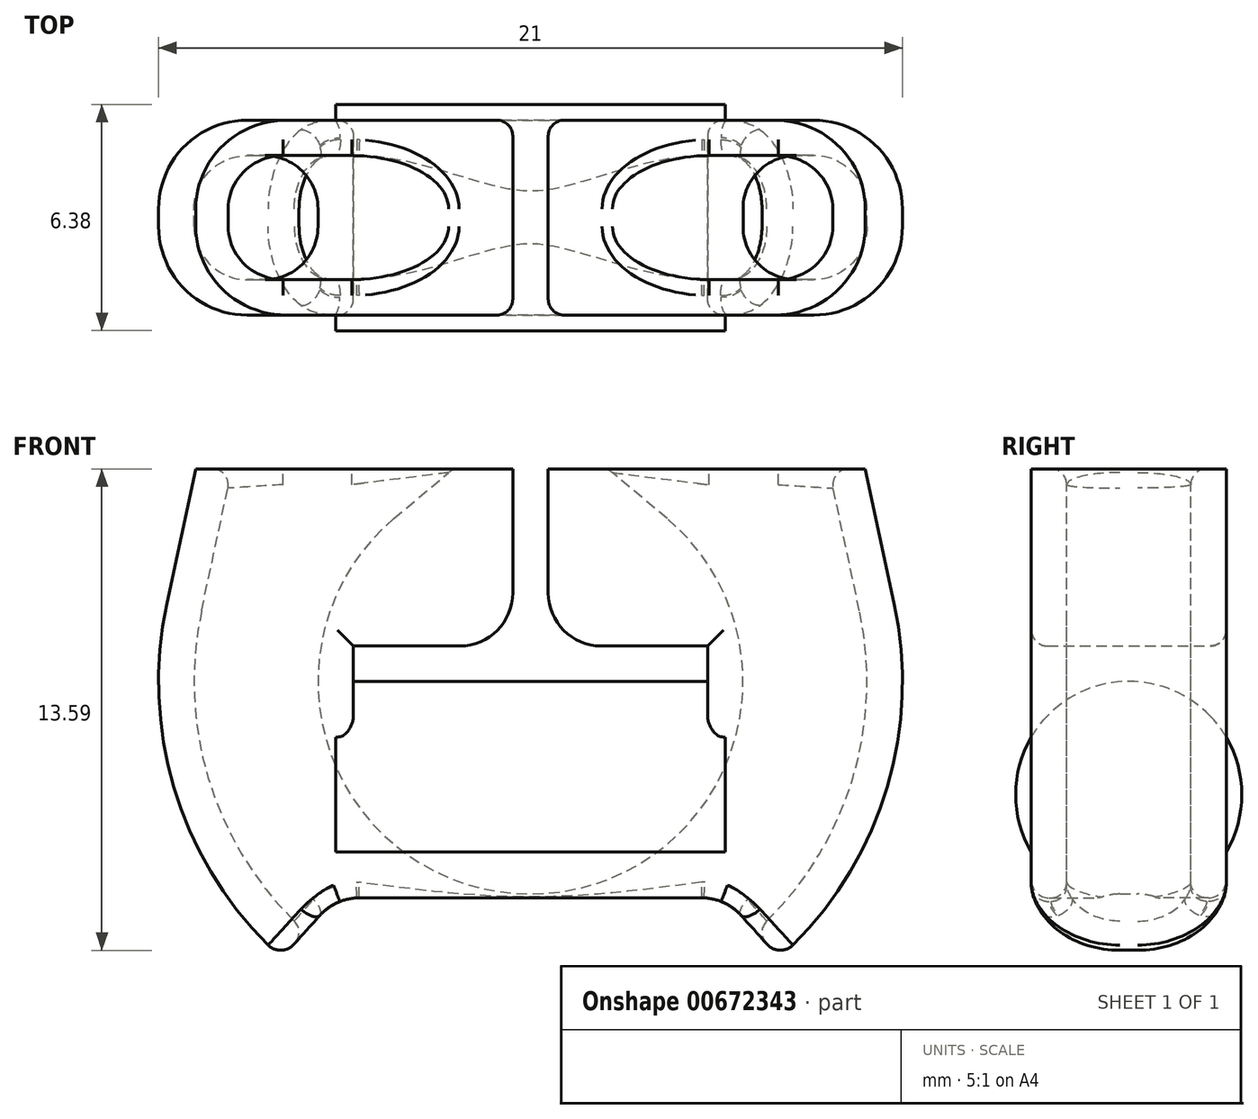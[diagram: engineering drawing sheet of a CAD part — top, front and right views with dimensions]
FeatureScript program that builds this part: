
annotation { "Feature Type Name" : "Feature", "Feature Type Description" : "" }
export const myFeature = defineFeature(function(context is Context, id is Id, definition is map)
    precondition{}
    {
        {
            var Q0;
            Q0=qCreatedBy(makeId("Front.planeOp"),FACE);
            var sketch = newSketch(context, id + "F0", { "sketchPlane" : qUnion([Q0])});
            skLineSegment(sketch, "E0.bottom", {"start": v(0, 0) * mm, "end": v(5, 0) * mm});
            skLineSegment(sketch, "E0.top", {"start": v(0, 1) * mm, "end": v(5, 1) * mm});
            skLineSegment(sketch, "E0.left", {"start": v(0, 0) * mm, "end": v(0, 1) * mm});
            skLineSegment(sketch, "E0.right", {"start": v(5, 0) * mm, "end": v(5, 1) * mm});
            skSolve(sketch);
        }
        {
            var Q0;
            Q0=qCreatedBy(makeId("Front.planeOp"),FACE);
            var sketch = newSketch(context, id + "F1", { "sketchPlane" : qUnion([Q0])});
            skArc(sketch, "E1", {"start": v(0, -10.5) * mm, "mid": v(8.17, -6.6) * mm, "end": v(10.27, 2.2) * mm});
            skLineSegment(sketch, "E2", {"start": v(10.27, 2.2) * mm, "end": v(9.45, 6) * mm});
            skLineSegment(sketch, "E3", {"start": v(9.45, 6) * mm, "end": v(0, 6) * mm});
            skLineSegment(sketch, "E4", {"start": v(0, 6) * mm, "end": v(0, -10.5) * mm});
            skPoint(sketch, "E5", {"position": v(10.5, 0) * mm});
            skPoint(sketch, "E6", {"position": v(0, 50) * mm});
            skSolve(sketch);
        }
        {
            var Q0;
            Q0=qSketchRegion(id+"F1",true);
            extrude(context, id + "F2", {"entities" : qUnion([Q0]), "depth" : 2.75 * mm, "offsetDistance" : 25 * mm});
        }
        {
            var Q0;
            Q0=qCreatedBy(makeId("Front.planeOp"),FACE);
            var sketch = newSketch(context, id + "F3", { "sketchPlane" : qUnion([Q0])});
            skArc(sketch, "E7", {"start": v(0, -6) * mm, "mid": v(5.64, -2.05) * mm, "end": v(3.86, 4.6) * mm});
            skArc(sketch, "E8.1", {"start": v(0, -9.5) * mm, "mid": v(7.39, -5.97) * mm, "end": v(9.29, 2) * mm});
            skLineSegment(sketch, "E9", {"start": v(9.29, 2) * mm, "end": v(8.43, 6) * mm});
            skLineSegment(sketch, "E10", {"start": v(3.86, 4.6) * mm, "end": v(2.18, 6) * mm});
            skPoint(sketch, "E11", {"position": v(6, 0) * mm});
            skPoint(sketch, "E12", {"position": v(9.5, 0) * mm});
            skLineSegment(sketch, "E13", {"start": v(0, -6) * mm, "end": v(0, -9.5) * mm});
            skLineSegment(sketch, "E14", {"start": v(2.18, 6) * mm, "end": v(8.43, 6) * mm});
            skSolve(sketch);
        }
        {
            var Q0;
            Q0=qSketchRegion(id+"F3",true);
            extrude(context, id + "F4", {"entities" : qUnion([Q0]), "operationType" : NewBodyOperationType.REMOVE, "depth" : 1.75 * mm, "offsetDistance" : 25 * mm});
        }
        {
            var Q0;
            Q0=qCreatedBy(makeId("Front.planeOp"),FACE);
            var sketch = newSketch(context, id + "F5", { "sketchPlane" : qUnion([Q0])});
            skLineSegment(sketch, "E15.0", {"start": v(0.5, 1) * mm, "end": v(5, 1) * mm});
            skPoint(sketch, "E16.0", {"position": v(5, 0) * mm});
            skLineSegment(sketch, "E17.0", {"start": v(5, 0) * mm, "end": v(5, 1) * mm});
            skLineSegment(sketch, "E18", {"start": v(0.5, 6) * mm, "end": v(0.5, 1) * mm});
            skLineSegment(sketch, "E19", {"start": v(0.5, 6) * mm, "end": v(0, 6) * mm});
            skLineSegment(sketch, "E20", {"start": v(0, 6) * mm, "end": v(0, 0) * mm});
            skPoint(sketch, "E21.orphan", {"position": v(0, 1) * mm});
            skLineSegment(sketch, "E22", {"start": v(5, 0) * mm, "end": v(5, -2) * mm});
            skLineSegment(sketch, "E23", {"start": v(5, -2) * mm, "end": v(0, -2) * mm});
            skLineSegment(sketch, "E24", {"start": v(0, -2) * mm, "end": v(0, 0) * mm});
            skSolve(sketch);
        }
        {
            var Q0;
            Q0=qSketchRegion(id+"F5",true);
            extrude(context, id + "F6", {"entities" : qUnion([Q0]), "operationType" : NewBodyOperationType.REMOVE, "endBound" : BoundingType.THROUGH_ALL, "depth" : 25 * mm, "offsetDistance" : 25 * mm});
        }
        {
            var Q0;
            Q0=qCreatedBy(makeId("Front.planeOp"),FACE);
            var sketch = newSketch(context, id + "F7", { "sketchPlane" : qUnion([Q0])});
            skArc(sketch, "E25", {"start": v(0, -12) * mm, "mid": v(4.3, -11.2) * mm, "end": v(8.03, -8.92) * mm});
            skLineSegment(sketch, "E26", {"start": v(8.03, -8.92) * mm, "end": v(5.5, -6.1) * mm});
            skLineSegment(sketch, "E27", {"start": v(0, -12) * mm, "end": v(0, -6.1) * mm});
            skLineSegment(sketch, "E28", {"start": v(5.5, -6.1) * mm, "end": v(0, -6.1) * mm});
            skSolve(sketch);
        }
        {
            var Q0;
            Q0=qSketchRegion(id+"F7",true);
            extrude(context, id + "F8", {"entities" : qUnion([Q0]), "operationType" : NewBodyOperationType.REMOVE, "endBound" : BoundingType.THROUGH_ALL, "depth" : 25 * mm, "offsetDistance" : 25 * mm});
        }
        {
            var Q0;
            Q0=qCreatedBy(makeId("Right.planeOp"),FACE);
            var sketch = newSketch(context, id + "F9", { "sketchPlane" : qUnion([Q0])});
            skCircle(sketch, "E29", {"center": v(0, -7.75) * mm, "radius": 1.75 * mm});
            skPoint(sketch, "E30", {"position": v(0, -6) * mm});
            skCircle(sketch, "E31", {"center": v(0, -3.2) * mm, "radius": 3.2 * mm});
            skLineSegment(sketch, "E32", {"start": v(0, -25) * mm, "end": v(-3.7, 0) * mm});
            skSolve(sketch);
        }
        {
            var Q0;
            Q0=qCreatedBy(makeId("Right.planeOp"),FACE);
            var sketch = newSketch(context, id + "F10", { "sketchPlane" : qUnion([Q0])});
            skPoint(sketch, "E33.orphan", {"position": v(-3.7, 0) * mm});
            skArc(sketch, "E34.0", {"start": v(0, 0) * mm, "mid": v(-2.88, -1.8) * mm, "end": v(-2.5, -5.18) * mm});
            skLineSegment(sketch, "E35", {"start": v(-2.5, -2.1) * mm, "end": v(-2.5, -5.18) * mm});
            skPoint(sketch, "E36.orphan", {"position": v(0, -25) * mm});
            skLineSegment(sketch, "E37", {"start": v(0, 0) * mm, "end": v(0, -2.1) * mm});
            skLineSegment(sketch, "E38", {"start": v(0, -2.1) * mm, "end": v(-2.5, -2.1) * mm});
            skSolve(sketch);
        }
        {
            var Q0;
            Q0 = qSketchRegion(id + "F10", true);
            extrude(context, id + "F11", {"entities" : qUnion([Q0]), "operationType" : NewBodyOperationType.ADD, "depth" : 5.5 * mm, "offsetDistance" : 25 * mm});
        }
        {
            var Q0;
            Q0=makeQuery(id+"F2.opExtrude","CAP_EDGE",EDGE,{"disambiguationData":[OSD([sQuery(id+"F1.wireOp",EDGE,"E1")])],"isStart":false});
            fillet(context, id + "F12", {"entities" : qUnion([Q0]), "radius" : 2.5 * mm, "tangentPropagation" : true, "allowEdgeOverflow" : false});
        }
        {
            var Q0;
            Q0=makeQuery(id+"F4.boolean.opBoolean","COPY",EDGE,{"derivedFrom":makeQuery(id+"F4.opExtrude","CAP_EDGE",EDGE,{"disambiguationData":[OSD([sQuery(id+"F3.wireOp",EDGE,"E8.1")])],"isStart":false})});
            var Q1;
            Q1=makeQuery(id+"F4.boolean.opBoolean","COPY",EDGE,{"derivedFrom":makeQuery(id+"F4.opExtrude","CAP_EDGE",EDGE,{"disambiguationData":[OSD([sQuery(id+"F3.wireOp",EDGE,"E7")])],"isStart":false})});
            fillet(context, id + "F13", {"entities" : qUnion([Q0, Q1]), "radius" : 1.5 * mm, "tangentPropagation" : true, "allowEdgeOverflow" : false});
        }
        {
            var Q0;
            Q0=makeQuery(id+"F6.boolean.opBoolean","COPY",EDGE,{"derivedFrom":makeQuery(id+"F6.opExtrude","SWEPT_EDGE",EDGE,{"disambiguationData":[OSD([sQuery(id+"F5.wireOp",EDGE,"E15.0"),sQuery(id+"F5.wireOp",EDGE,"E18")])]})});
            var Q1;
            Q1=makeQuery(id+"F6.boolean.opBoolean","COPY",EDGE,{"derivedFrom":makeQuery(id+"F6.opExtrude","SWEPT_EDGE",EDGE,{"disambiguationData":[OSD([sQuery(id+"F5.wireOp",EDGE,"E18"),sQuery(id+"F5.wireOp",EDGE,"E19")])]})});
            var Q2;
            Q2=makeQuery(id+"F8.boolean.opBoolean","COPY",EDGE,{"derivedFrom":makeQuery(id+"F8.opExtrude","SWEPT_EDGE",EDGE,{"disambiguationData":[OSD([sQuery(id+"F7.wireOp",EDGE,"GExpFUsB-Pr3Z-94vW-ss1V-Dc07WEOKBbOR"),sQuery(id+"F7.wireOp",EDGE,"E26")])]})});
            fillet(context, id + "F14", {"entities" : qUnion([Q0, Q1, Q2]), "radius" : 1.5 * mm, "tangentPropagation" : true, "allowEdgeOverflow" : false});
        }
        {
            var Q0;
            Q0=makeQuery(id+"F6.boolean.opBoolean","INTERSECT",EDGE,{"derivedFrom":[makeQuery(id+"F2.opExtrude","CAP_FACE",FACE,{"disambiguationData":[OSD([sQuery(id+"F1.wireOp",EDGE,"E1"),sQuery(id+"F1.wireOp",EDGE,"E2"),sQuery(id+"F1.wireOp",EDGE,"E3"),sQuery(id+"F1.wireOp",EDGE,"E4")])],"isStart":false}),makeQuery(id+"F6.opExtrude","SWEPT_FACE",FACE,{"disambiguationData":[OSD([sQuery(id+"F5.wireOp",EDGE,"E15.0")])]})]});
            var Q1;
            Q1=makeQuery(id+"F11.boolean.opBoolean","SPLIT",EDGE,{"derivedFrom":makeQuery(id+"F6.boolean.opBoolean","INTERSECT",EDGE,{"derivedFrom":[makeQuery(id+"F2.opExtrude","CAP_FACE",FACE,{"disambiguationData":[OSD([sQuery(id+"F1.wireOp",EDGE,"E1"),sQuery(id+"F1.wireOp",EDGE,"E2"),sQuery(id+"F1.wireOp",EDGE,"E3"),sQuery(id+"F1.wireOp",EDGE,"E4")])],"isStart":false}),makeQuery(id+"F6.opExtrude","SWEPT_FACE",FACE,{"disambiguationData":[OSD([sQuery(id+"F5.wireOp",EDGE,"E17.0"),sQuery(id+"F5.wireOp",EDGE,"E22")])]})]})});
            var Q2;
            Q2=makeQuery(id+"F13.opFillet","BLEND_EDGE",EDGE,{"blendedFrom":[makeQuery(id+"F4.boolean.opBoolean","COPY",EDGE,{"derivedFrom":makeQuery(id+"F4.opExtrude","CAP_EDGE",EDGE,{"disambiguationData":[OSD([sQuery(id+"F3.wireOp",EDGE,"E9")])],"isStart":false})}),makeQuery(id+"F2.opExtrude","SWEPT_FACE",FACE,{"disambiguationData":[OSD([sQuery(id+"F1.wireOp",EDGE,"E3")])]})],"blendedInto":[makeQuery(id+"F2.opExtrude","SWEPT_FACE",FACE,{"disambiguationData":[OSD([sQuery(id+"F1.wireOp",EDGE,"E3")])]})]});
            var Q3;
            Q3=makeQuery(id+"F13.opFillet","BLEND_EDGE",EDGE,{"blendedFrom":[makeQuery(id+"F4.boolean.opBoolean","COPY",EDGE,{"derivedFrom":makeQuery(id+"F4.opExtrude","CAP_EDGE",EDGE,{"disambiguationData":[OSD([sQuery(id+"F3.wireOp",EDGE,"E7")])],"isStart":false})}),makeQuery(id+"F8.boolean.opBoolean","COPY",FACE,{"derivedFrom":makeQuery(id+"F8.opExtrude","SWEPT_FACE",FACE,{"disambiguationData":[OSD([sQuery(id+"F7.wireOp",EDGE,"E28")])]})})],"blendedInto":[makeQuery(id+"F8.boolean.opBoolean","COPY",FACE,{"derivedFrom":makeQuery(id+"F8.opExtrude","SWEPT_FACE",FACE,{"disambiguationData":[OSD([sQuery(id+"F7.wireOp",EDGE,"E28")])]})})]});
            fillet(context, id + "F15", {"entities" : qUnion([Q0, Q1, Q2, Q3]), "radius" : 0.45 * mm, "tangentPropagation" : true, "allowEdgeOverflow" : false});
        }
        {
            var Q0;
            Q0=makeQuery(id+"F8.boolean.opBoolean","INTERSECT",EDGE,{"derivedFrom":[makeQuery(id+"F2.opExtrude","CAP_FACE",FACE,{"disambiguationData":[OSD([sQuery(id+"F1.wireOp",EDGE,"E1"),sQuery(id+"F1.wireOp",EDGE,"E2"),sQuery(id+"F1.wireOp",EDGE,"E3"),sQuery(id+"F1.wireOp",EDGE,"E4")])],"isStart":false}),makeQuery(id+"F8.opExtrude","SWEPT_FACE",FACE,{"disambiguationData":[OSD([sQuery(id+"F7.wireOp",EDGE,"E28")])]})]});
            fillet(context, id + "F16", {"entities" : qUnion([Q0]), "radius" : 0.5 * mm, "tangentPropagation" : true, "allowEdgeOverflow" : false});
        }
        {
            var Q0;
            Q0=makeQuery(id+"F2.opExtrude","SWEPT_BODY",BODY,{"disambiguationData":[OSD([sQuery(id+"F1.wireOp",EDGE,"E1"),sQuery(id+"F1.wireOp",EDGE,"E2"),sQuery(id+"F1.wireOp",EDGE,"E3"),sQuery(id+"F1.wireOp",EDGE,"E4")])]});
            var Q1;
            Q1=qCreatedBy(makeId("Front.planeOp"),FACE);
            mirror(context, id + "F17", {"operationType" : NewBodyOperationType.ADD, "entities" : qUnion([Q0]), "mirrorPlane" : qUnion([Q1])});
        }
        {
            var Q0;
            Q0=makeQuery(id+"F2.opExtrude","SWEPT_BODY",BODY,{"disambiguationData":[OSD([sQuery(id+"F1.wireOp",EDGE,"E1"),sQuery(id+"F1.wireOp",EDGE,"E2"),sQuery(id+"F1.wireOp",EDGE,"E3"),sQuery(id+"F1.wireOp",EDGE,"E4")])]});
            var Q1;
            Q1=qCreatedBy(makeId("Right.planeOp"),FACE);
            mirror(context, id + "F18", {"operationType" : NewBodyOperationType.ADD, "entities" : qUnion([Q0]), "mirrorPlane" : qUnion([Q1])});
        }
    });
